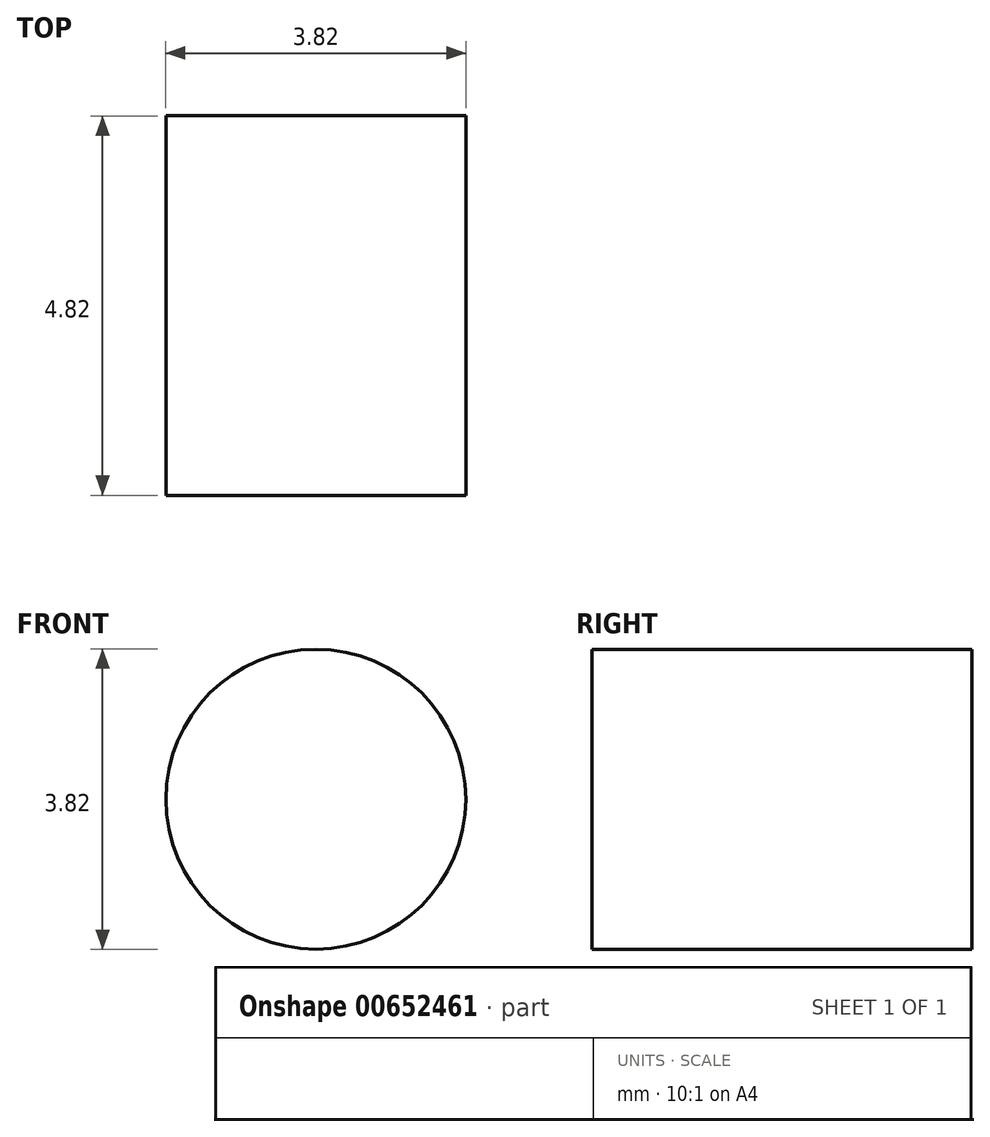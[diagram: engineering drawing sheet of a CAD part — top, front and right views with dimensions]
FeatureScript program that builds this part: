
annotation { "Feature Type Name" : "Feature", "Feature Type Description" : "" }
export const myFeature = defineFeature(function(context is Context, id is Id, definition is map)
    precondition{}
    {
        {
            var Q0;
            Q0=qCreatedBy(makeId("Front.planeOp"),FACE);
            var sketch = newSketch(context, id + "F0", { "sketchPlane" : qUnion([Q0])});
            skCircle(sketch, "E0", {"center": v(0, 0) * mm, "radius": 1.9 * mm});
            skSolve(sketch);
        }
        {
            var Q0;
            Q0 = qSketchRegion(id + "F0", true);
            extrude(context, id + "F1", {"entities" : qUnion([Q0]), "endBound" : BoundingType.SYMMETRIC, "depth" : 4.83 * mm, "offsetDistance" : 25.4 * mm});
        }
    });
